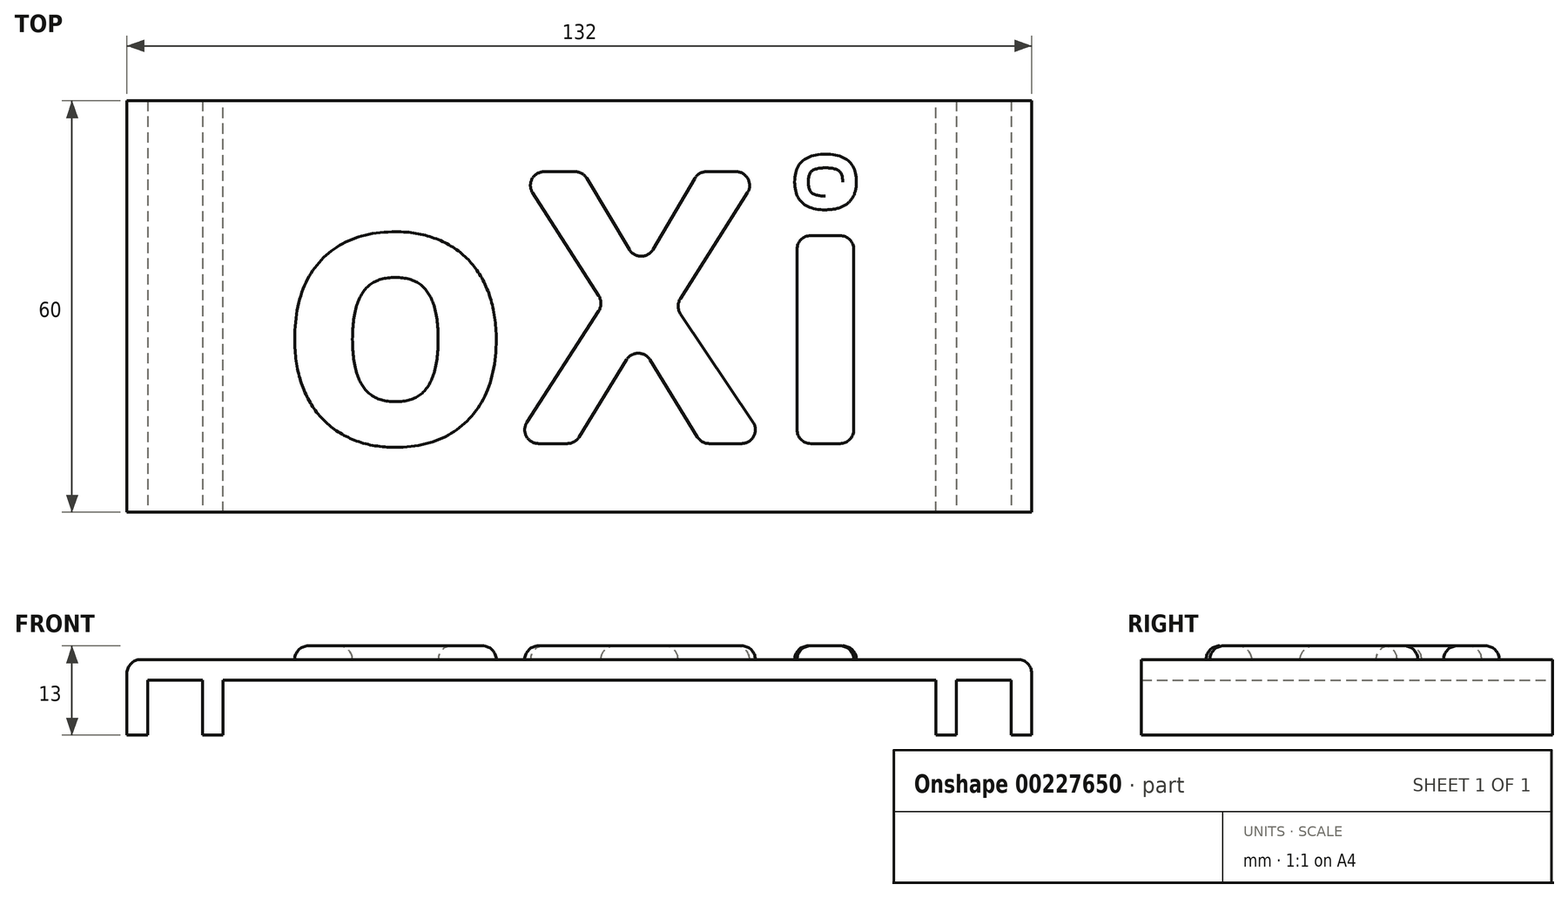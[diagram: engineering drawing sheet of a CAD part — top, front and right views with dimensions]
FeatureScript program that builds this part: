
annotation { "Feature Type Name" : "Feature", "Feature Type Description" : "" }
export const myFeature = defineFeature(function(context is Context, id is Id, definition is map)
    precondition{}
    {
        {
            var Q0;
            Q0=qCreatedBy(makeId("Top.planeOp"),FACE);
            var sketch = newSketch(context, id + "F0", { "sketchPlane" : qUnion([Q0])});
            skLineSegment(sketch, "E0.bottom", {"start": v(52, -30) * mm, "end": v(-52, -30) * mm});
            skLineSegment(sketch, "E0.top", {"start": v(52, 30) * mm, "end": v(-52, 30) * mm});
            skLineSegment(sketch, "E0.left", {"start": v(52, -30) * mm, "end": v(52, 30) * mm});
            skLineSegment(sketch, "E0.right", {"start": v(-52, -30) * mm, "end": v(-52, 30) * mm});
            skPoint(sketch, "E0.middle", {"position": v(0, 0) * mm});
            skLineSegment(sketch, "E1", {"start": v(-52, 30) * mm, "end": v(-55, 30) * mm});
            skLineSegment(sketch, "E2", {"start": v(-55, 30) * mm, "end": v(-55, -30) * mm});
            skLineSegment(sketch, "E3", {"start": v(-55, -30) * mm, "end": v(-52, -30) * mm});
            skLineSegment(sketch, "E4", {"start": v(52, 30) * mm, "end": v(55, 30) * mm});
            skLineSegment(sketch, "E5", {"start": v(55, 30) * mm, "end": v(55, -30) * mm});
            skLineSegment(sketch, "E6", {"start": v(55, -30) * mm, "end": v(52, -30) * mm});
            skLineSegment(sketch, "E7", {"start": v(-55, 30) * mm, "end": v(-63, 30) * mm});
            skLineSegment(sketch, "E8", {"start": v(-63, 30) * mm, "end": v(-63, -30) * mm});
            skLineSegment(sketch, "E9", {"start": v(-63, -30) * mm, "end": v(-55, -30) * mm});
            skLineSegment(sketch, "E10", {"start": v(-63, 30) * mm, "end": v(-66, 30) * mm});
            skLineSegment(sketch, "E11", {"start": v(-66, 30) * mm, "end": v(-66, -30) * mm});
            skLineSegment(sketch, "E12", {"start": v(-66, -30) * mm, "end": v(-63, -30) * mm});
            skLineSegment(sketch, "E13", {"start": v(55, 30) * mm, "end": v(63, 30) * mm});
            skLineSegment(sketch, "E14", {"start": v(63, 30) * mm, "end": v(63, -30) * mm});
            skLineSegment(sketch, "E15", {"start": v(63, -30) * mm, "end": v(55, -30) * mm});
            skLineSegment(sketch, "E16", {"start": v(63, 30) * mm, "end": v(66, 30) * mm});
            skLineSegment(sketch, "E17", {"start": v(66, 30) * mm, "end": v(66, -30) * mm});
            skLineSegment(sketch, "E18", {"start": v(66, -30) * mm, "end": v(63, -30) * mm});
            skSolve(sketch);
        }
        {
            var Q0;
            Q0=makeQuery(id+"F0.imprint","IMPRINT",FACE,{"disambiguationData":[TD([[makeQuery(id+"F0.imprint","IMPRINT",EDGE,{"derivedFrom":sQuery(id+"F0.wireOp",EDGE,"E8")}),-1.0]])]});
            var Q1;
            Q1=makeQuery(id+"F0.imprint","IMPRINT",FACE,{"disambiguationData":[TD([[makeQuery(id+"F0.imprint","IMPRINT",EDGE,{"derivedFrom":sQuery(id+"F0.wireOp",EDGE,"E0.right")}),1.0]])]});
            var Q2;
            Q2=makeQuery(id+"F0.imprint","IMPRINT",FACE,{"disambiguationData":[TD([[makeQuery(id+"F0.imprint","IMPRINT",EDGE,{"derivedFrom":sQuery(id+"F0.wireOp",EDGE,"E0.left")}),-1.0]])]});
            var Q3;
            Q3=makeQuery(id+"F0.imprint","IMPRINT",FACE,{"disambiguationData":[TD([[makeQuery(id+"F0.imprint","IMPRINT",EDGE,{"derivedFrom":sQuery(id+"F0.wireOp",EDGE,"E14")}),1.0]])]});
            extrude(context, id + "F1", {"entities" : qUnion([Q0, Q1, Q2, Q3]), "oppositeDirection" : true, "depth" : 11 * mm});
        }
        {
            var Q0;
            Q0=makeQuery(id+"F0.imprint","IMPRINT",FACE,{"disambiguationData":[TD([[makeQuery(id+"F0.imprint","IMPRINT",EDGE,{"derivedFrom":sQuery(id+"F0.wireOp",EDGE,"E2")}),-1.0]])]});
            var Q1;
            Q1=makeQuery(id+"F0.imprint","IMPRINT",FACE,{"disambiguationData":[TD([[makeQuery(id+"F0.imprint","IMPRINT",EDGE,{"derivedFrom":sQuery(id+"F0.wireOp",EDGE,"E5")}),1.0]])]});
            var Q2;
            Q2=makeQuery(id+"F0.imprint","IMPRINT",FACE,{"disambiguationData":[TD([[makeQuery(id+"F0.imprint","IMPRINT",EDGE,{"derivedFrom":sQuery(id+"F0.wireOp",EDGE,"E0.bottom")}),-1.0]])]});
            extrude(context, id + "F2", {"entities" : qUnion([Q0, Q1, Q2]), "operationType" : NewBodyOperationType.ADD, "oppositeDirection" : true, "depth" : 3 * mm});
        }
        {
            var Q0;
            Q0=makeQuery(id+"F0.imprint","IMPRINT",FACE,{"disambiguationData":[TD([[makeQuery(id+"F0.imprint","IMPRINT",EDGE,{"derivedFrom":sQuery(id+"F0.wireOp",EDGE,"E0.bottom")}),-1.0]])]});
            var sketch = newSketch(context, id + "F3", { "sketchPlane" : qUnion([Q0])});
            skText(sketch, "E19", { "text": "oXi", "fontName": "OpenSans-Bold.ttf"});
            const initialGuessF3  = {"E19": [-0.04403, -0.02, 1, 0, 0.04]};
            skSetInitialGuess(sketch, initialGuessF3);
            skSolve(sketch);
        }
        {
            var Q0;
            Q0=makeQuery(id+"F3.imprint","IMPRINT",FACE,{"disambiguationData":[TD([[makeQuery(id+"F3.imprint","IMPRINT",EDGE,{"derivedFrom":sQuery(id+"F3.wireOp",EDGE,"E19.sketch_text.stroke-0")}),-1.0]])]});
            var Q1;
            Q1=makeQuery(id+"F3.imprint","IMPRINT",FACE,{"disambiguationData":[TD([[makeQuery(id+"F3.imprint","IMPRINT",EDGE,{"derivedFrom":sQuery(id+"F3.wireOp",EDGE,"E19.sketch_text.stroke-18")}),-1.0]])]});
            var Q2;
            Q2=makeQuery(id+"F3.imprint","IMPRINT",FACE,{"disambiguationData":[TD([[makeQuery(id+"F3.imprint","IMPRINT",EDGE,{"derivedFrom":sQuery(id+"F3.wireOp",EDGE,"E19.sketch_text.stroke-35")}),-1.0]])]});
            var Q3;
            Q3=makeQuery(id+"F3.imprint","IMPRINT",FACE,{"disambiguationData":[TD([[makeQuery(id+"F3.imprint","IMPRINT",EDGE,{"derivedFrom":sQuery(id+"F3.wireOp",EDGE,"E19.sketch_text.stroke-30")}),-1.0]])]});
            extrude(context, id + "F4", {"entities" : qUnion([Q0, Q1, Q2, Q3]), "operationType" : NewBodyOperationType.ADD, "depth" : 2 * mm});
        }
        {
            var Q0;
            Q0=makeQuery(id+"F1.opExtrude","CAP_EDGE",EDGE,{"disambiguationData":[OSD([sQuery(id+"F0.wireOp",EDGE,"E11")])],"isStart":true});
            var Q1;
            Q1=makeQuery(id+"F1.opExtrude","CAP_EDGE",EDGE,{"disambiguationData":[OSD([sQuery(id+"F0.wireOp",EDGE,"E17")])],"isStart":true});
            fillet(context, id + "F5", {"entities" : qUnion([Q0, Q1]), "radius" : 2 * mm, "tangentPropagation" : true, "allowEdgeOverflow" : false});
        }
        {
            var Q0;
            Q0=makeQuery(id+"F4.opExtrude","CAP_EDGE",EDGE,{"disambiguationData":[OSD([sQuery(id+"F3.wireOp",EDGE,"E19.sketch_text.stroke-12")])],"isStart":false});
            var Q1;
            Q1=makeQuery(id+"F4.opExtrude","CAP_EDGE",EDGE,{"disambiguationData":[OSD([sQuery(id+"F3.wireOp",EDGE,"E19.sketch_text.stroke-0")])],"isStart":false});
            var Q2;
            Q2=makeQuery(id+"F4.opExtrude","CAP_EDGE",EDGE,{"disambiguationData":[OSD([sQuery(id+"F3.wireOp",EDGE,"E19.sketch_text.stroke-22")])],"isStart":false});
            var Q3;
            Q3=makeQuery(id+"F4.opExtrude","CAP_EDGE",EDGE,{"disambiguationData":[OSD([sQuery(id+"F3.wireOp",EDGE,"E19.sketch_text.stroke-20")])],"isStart":false});
            var Q4;
            Q4=makeQuery(id+"F4.opExtrude","CAP_EDGE",EDGE,{"disambiguationData":[OSD([sQuery(id+"F3.wireOp",EDGE,"E19.sketch_text.stroke-21")])],"isStart":false});
            var Q5;
            Q5=makeQuery(id+"F4.opExtrude","CAP_EDGE",EDGE,{"disambiguationData":[OSD([sQuery(id+"F3.wireOp",EDGE,"E19.sketch_text.stroke-19")])],"isStart":false});
            var Q6;
            Q6=makeQuery(id+"F4.opExtrude","CAP_EDGE",EDGE,{"disambiguationData":[OSD([sQuery(id+"F3.wireOp",EDGE,"E19.sketch_text.stroke-29")])],"isStart":false});
            var Q7;
            Q7=makeQuery(id+"F4.opExtrude","CAP_EDGE",EDGE,{"disambiguationData":[OSD([sQuery(id+"F3.wireOp",EDGE,"E19.sketch_text.stroke-18")])],"isStart":false});
            var Q8;
            Q8=makeQuery(id+"F4.opExtrude","CAP_EDGE",EDGE,{"disambiguationData":[OSD([sQuery(id+"F3.wireOp",EDGE,"E19.sketch_text.stroke-28")])],"isStart":false});
            var Q9;
            Q9=makeQuery(id+"F4.opExtrude","CAP_EDGE",EDGE,{"disambiguationData":[OSD([sQuery(id+"F3.wireOp",EDGE,"E19.sketch_text.stroke-26")])],"isStart":false});
            var Q10;
            Q10=makeQuery(id+"F4.opExtrude","CAP_EDGE",EDGE,{"disambiguationData":[OSD([sQuery(id+"F3.wireOp",EDGE,"E19.sketch_text.stroke-25")])],"isStart":false});
            var Q11;
            Q11=makeQuery(id+"F4.opExtrude","CAP_EDGE",EDGE,{"disambiguationData":[OSD([sQuery(id+"F3.wireOp",EDGE,"E19.sketch_text.stroke-23")])],"isStart":false});
            var Q12;
            Q12=makeQuery(id+"F4.opExtrude","CAP_EDGE",EDGE,{"disambiguationData":[OSD([sQuery(id+"F3.wireOp",EDGE,"E19.sketch_text.stroke-24")])],"isStart":false});
            var Q13;
            Q13=makeQuery(id+"F4.opExtrude","CAP_EDGE",EDGE,{"disambiguationData":[OSD([sQuery(id+"F3.wireOp",EDGE,"E19.sketch_text.stroke-27")])],"isStart":false});
            var Q14;
            Q14=makeQuery(id+"F4.opExtrude","SWEPT_EDGE",EDGE,{"disambiguationData":[OSD([sQuery(id+"F3.wireOp",EDGE,"E19.sketch_text.stroke-27"),sQuery(id+"F3.wireOp",EDGE,"E19.sketch_text.stroke-28")])]});
            var Q15;
            Q15=makeQuery(id+"F4.opExtrude","SWEPT_EDGE",EDGE,{"disambiguationData":[OSD([sQuery(id+"F3.wireOp",EDGE,"E19.sketch_text.stroke-26"),sQuery(id+"F3.wireOp",EDGE,"E19.sketch_text.stroke-27")])]});
            var Q16;
            Q16=makeQuery(id+"F4.opExtrude","SWEPT_EDGE",EDGE,{"disambiguationData":[OSD([sQuery(id+"F3.wireOp",EDGE,"E19.sketch_text.stroke-24"),sQuery(id+"F3.wireOp",EDGE,"E19.sketch_text.stroke-25")])]});
            var Q17;
            Q17=makeQuery(id+"F4.opExtrude","SWEPT_EDGE",EDGE,{"disambiguationData":[OSD([sQuery(id+"F3.wireOp",EDGE,"E19.sketch_text.stroke-23"),sQuery(id+"F3.wireOp",EDGE,"E19.sketch_text.stroke-24")])]});
            var Q18;
            Q18=makeQuery(id+"F4.opExtrude","SWEPT_EDGE",EDGE,{"disambiguationData":[OSD([sQuery(id+"F3.wireOp",EDGE,"E19.sketch_text.stroke-25"),sQuery(id+"F3.wireOp",EDGE,"E19.sketch_text.stroke-26")])]});
            var Q19;
            Q19=makeQuery(id+"F4.opExtrude","SWEPT_EDGE",EDGE,{"disambiguationData":[OSD([sQuery(id+"F3.wireOp",EDGE,"E19.sketch_text.stroke-19"),sQuery(id+"F3.wireOp",EDGE,"E19.sketch_text.stroke-20")])]});
            var Q20;
            Q20=makeQuery(id+"F4.opExtrude","SWEPT_EDGE",EDGE,{"disambiguationData":[OSD([sQuery(id+"F3.wireOp",EDGE,"E19.sketch_text.stroke-28"),sQuery(id+"F3.wireOp",EDGE,"E19.sketch_text.stroke-29")])]});
            var Q21;
            Q21=makeQuery(id+"F4.opExtrude","SWEPT_EDGE",EDGE,{"disambiguationData":[OSD([sQuery(id+"F3.wireOp",EDGE,"E19.sketch_text.stroke-22"),sQuery(id+"F3.wireOp",EDGE,"E19.sketch_text.stroke-23")])]});
            var Q22;
            Q22=makeQuery(id+"F4.opExtrude","SWEPT_EDGE",EDGE,{"disambiguationData":[OSD([sQuery(id+"F3.wireOp",EDGE,"E19.sketch_text.stroke-21"),sQuery(id+"F3.wireOp",EDGE,"E19.sketch_text.stroke-22")])]});
            var Q23;
            Q23=makeQuery(id+"F4.opExtrude","SWEPT_EDGE",EDGE,{"disambiguationData":[OSD([sQuery(id+"F3.wireOp",EDGE,"E19.sketch_text.stroke-20"),sQuery(id+"F3.wireOp",EDGE,"E19.sketch_text.stroke-21")])]});
            var Q24;
            Q24=makeQuery(id+"F4.opExtrude","SWEPT_EDGE",EDGE,{"disambiguationData":[OSD([sQuery(id+"F3.wireOp",EDGE,"E19.sketch_text.stroke-18"),sQuery(id+"F3.wireOp",EDGE,"E19.sketch_text.stroke-19")])]});
            var Q25;
            Q25=makeQuery(id+"F4.opExtrude","SWEPT_EDGE",EDGE,{"disambiguationData":[OSD([sQuery(id+"F3.wireOp",EDGE,"E19.sketch_text.stroke-18"),sQuery(id+"F3.wireOp",EDGE,"E19.sketch_text.stroke-29")])]});
            var Q26;
            Q26=makeQuery(id+"F4.opExtrude","SWEPT_EDGE",EDGE,{"disambiguationData":[OSD([sQuery(id+"F3.wireOp",EDGE,"E19.sketch_text.stroke-35"),sQuery(id+"F3.wireOp",EDGE,"E19.sketch_text.stroke-36")])]});
            var Q27;
            Q27=makeQuery(id+"F4.opExtrude","SWEPT_EDGE",EDGE,{"disambiguationData":[OSD([sQuery(id+"F3.wireOp",EDGE,"E19.sketch_text.stroke-35"),sQuery(id+"F3.wireOp",EDGE,"E19.sketch_text.stroke-38")])]});
            var Q28;
            Q28=makeQuery(id+"F4.opExtrude","CAP_EDGE",EDGE,{"disambiguationData":[OSD([sQuery(id+"F3.wireOp",EDGE,"E19.sketch_text.stroke-38")])],"isStart":false});
            var Q29;
            Q29=makeQuery(id+"F4.opExtrude","CAP_EDGE",EDGE,{"disambiguationData":[OSD([sQuery(id+"F3.wireOp",EDGE,"E19.sketch_text.stroke-35")])],"isStart":false});
            var Q30;
            Q30=makeQuery(id+"F4.opExtrude","CAP_EDGE",EDGE,{"disambiguationData":[OSD([sQuery(id+"F3.wireOp",EDGE,"E19.sketch_text.stroke-36")])],"isStart":false});
            var Q31;
            Q31=makeQuery(id+"F4.opExtrude","CAP_EDGE",EDGE,{"disambiguationData":[OSD([sQuery(id+"F3.wireOp",EDGE,"E19.sketch_text.stroke-37")])],"isStart":false});
            var Q32;
            Q32=makeQuery(id+"F4.opExtrude","CAP_EDGE",EDGE,{"disambiguationData":[OSD([sQuery(id+"F3.wireOp",EDGE,"E19.sketch_text.stroke-33")])],"isStart":false});
            var Q33;
            Q33=makeQuery(id+"F4.opExtrude","SWEPT_EDGE",EDGE,{"disambiguationData":[OSD([sQuery(id+"F3.wireOp",EDGE,"E19.sketch_text.stroke-37"),sQuery(id+"F3.wireOp",EDGE,"E19.sketch_text.stroke-38")])]});
            var Q34;
            Q34=makeQuery(id+"F4.opExtrude","SWEPT_EDGE",EDGE,{"disambiguationData":[OSD([sQuery(id+"F3.wireOp",EDGE,"E19.sketch_text.stroke-36"),sQuery(id+"F3.wireOp",EDGE,"E19.sketch_text.stroke-37")])]});
            fillet(context, id + "F6", {"entities" : qUnion([Q0, Q1, Q2, Q3, Q4, Q5, Q6, Q7, Q8, Q9, Q10, Q11, Q12, Q13, Q14, Q15, Q16, Q17, Q18, Q19, Q20, Q21, Q22, Q23, Q24, Q25, Q26, Q27, Q28, Q29, Q30, Q31, Q32, Q33, Q34]), "radius" : 2 * mm, "tangentPropagation" : true, "allowEdgeOverflow" : false});
        }
    });
